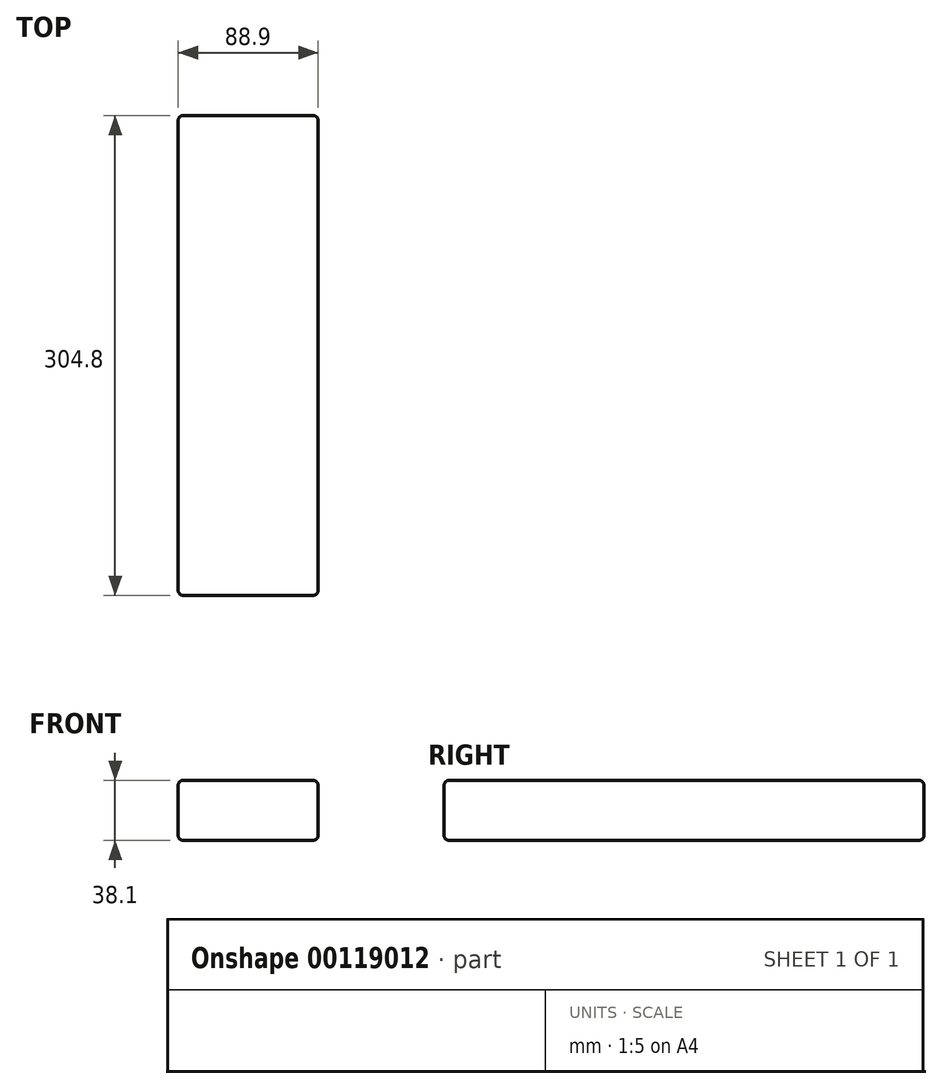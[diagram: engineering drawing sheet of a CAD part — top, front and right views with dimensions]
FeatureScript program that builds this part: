
annotation { "Feature Type Name" : "Feature", "Feature Type Description" : "" }
export const myFeature = defineFeature(function(context is Context, id is Id, definition is map)
    precondition{}
    {
        {
            var Q0;
            Q0=qCreatedBy(makeId("Right.planeOp"),FACE);
            var sketch = newSketch(context, id + "F0", { "sketchPlane" : qUnion([Q0])});
            skLineSegment(sketch, "E0.bottom", {"start": v(0, 0) * mm, "end": v(304.8, 0) * mm});
            skLineSegment(sketch, "E0.top", {"start": v(0, 38.1) * mm, "end": v(304.8, 38.1) * mm});
            skLineSegment(sketch, "E0.left", {"start": v(0, 0) * mm, "end": v(0, 38.1) * mm});
            skLineSegment(sketch, "E0.right", {"start": v(304.8, 0) * mm, "end": v(304.8, 38.1) * mm});
            skSolve(sketch);
        }
        {
            var Q0;
            Q0=makeQuery(id+"F0.imprint","IMPRINT",FACE,{"disambiguationData":[TD([[makeQuery(id+"F0.imprint","IMPRINT",EDGE,{"derivedFrom":sQuery(id+"F0.wireOp",EDGE,"E0.bottom")}),1.0]])]});
            extrude(context, id + "F1", {"entities" : qUnion([Q0]), "oppositeDirection" : true, "depth" : 88.9 * mm});
        }
        {
            var Q0;
            Q0=makeQuery(id+"F1.opExtrude","CAP_EDGE",EDGE,{"disambiguationData":[OSD([sQuery(id+"F0.wireOp",EDGE,"E0.top")])],"isStart":false});
            var Q1;
            Q1=makeQuery(id+"F1.opExtrude","SWEPT_EDGE",EDGE,{"disambiguationData":[OSD([sQuery(id+"F0.wireOp",EDGE,"E0.top"),sQuery(id+"F0.wireOp",EDGE,"E0.left")])]});
            var Q2;
            Q2=makeQuery(id+"F1.opExtrude","CAP_EDGE",EDGE,{"disambiguationData":[OSD([sQuery(id+"F0.wireOp",EDGE,"E0.top")])],"isStart":true});
            var Q3;
            Q3=makeQuery(id+"F1.opExtrude","SWEPT_EDGE",EDGE,{"disambiguationData":[OSD([sQuery(id+"F0.wireOp",EDGE,"E0.top"),sQuery(id+"F0.wireOp",EDGE,"E0.right")])]});
            var Q4;
            Q4=makeQuery(id+"F1.opExtrude","CAP_EDGE",EDGE,{"disambiguationData":[OSD([sQuery(id+"F0.wireOp",EDGE,"E0.left")])],"isStart":false});
            var Q5;
            Q5=makeQuery(id+"F1.opExtrude","CAP_EDGE",EDGE,{"disambiguationData":[OSD([sQuery(id+"F0.wireOp",EDGE,"E0.left")])],"isStart":true});
            var Q6;
            Q6=makeQuery(id+"F1.opExtrude","CAP_EDGE",EDGE,{"disambiguationData":[OSD([sQuery(id+"F0.wireOp",EDGE,"E0.bottom")])],"isStart":true});
            var Q7;
            Q7=makeQuery(id+"F1.opExtrude","SWEPT_EDGE",EDGE,{"disambiguationData":[OSD([sQuery(id+"F0.wireOp",EDGE,"E0.bottom"),sQuery(id+"F0.wireOp",EDGE,"E0.left")])]});
            var Q8;
            Q8=makeQuery(id+"F1.opExtrude","SWEPT_FACE",FACE,{"disambiguationData":[OSD([sQuery(id+"F0.wireOp",EDGE,"E0.right")])]});
            var Q9;
            Q9=makeQuery(id+"F1.opExtrude","SWEPT_FACE",FACE,{"disambiguationData":[OSD([sQuery(id+"F0.wireOp",EDGE,"E0.bottom")])]});
            fillet(context, id + "F2", {"entities" : qUnion([Q0, Q1, Q2, Q3, Q4, Q5, Q6, Q7, Q8, Q9]), "radius" : 3.17 * mm, "tangentPropagation" : true, "allowEdgeOverflow" : false});
        }
    });
